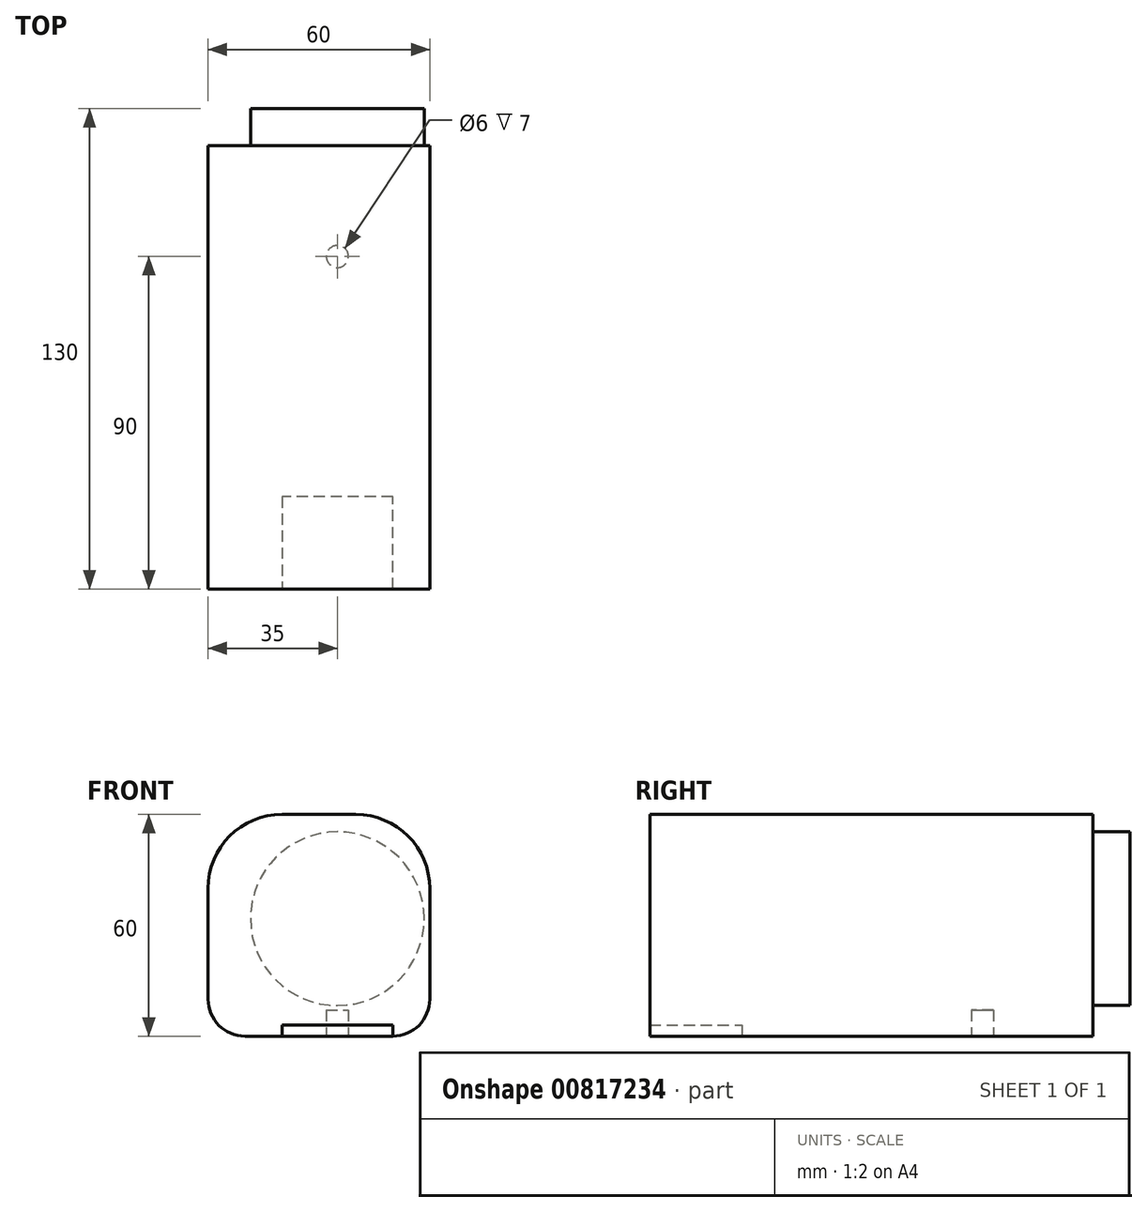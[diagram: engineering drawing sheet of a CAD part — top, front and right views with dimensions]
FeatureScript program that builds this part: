
annotation { "Feature Type Name" : "Feature", "Feature Type Description" : "" }
export const myFeature = defineFeature(function(context is Context, id is Id, definition is map)
    precondition{}
    {
        {
            var Q0;
            Q0=qCreatedBy(makeId("Top.planeOp"),FACE);
            var sketch = newSketch(context, id + "F0", { "sketchPlane" : qUnion([Q0])});
            skLineSegment(sketch, "E0.bottom", {"start": v(30, -60) * mm, "end": v(-30, -60) * mm});
            skLineSegment(sketch, "E0.top", {"start": v(30, 60) * mm, "end": v(-30, 60) * mm});
            skLineSegment(sketch, "E0.left", {"start": v(30, -60) * mm, "end": v(30, 60) * mm});
            skLineSegment(sketch, "E0.right", {"start": v(-30, -60) * mm, "end": v(-30, 60) * mm});
            skPoint(sketch, "E0.middle", {"position": v(0, 0) * mm});
            skSolve(sketch);
        }
        {
            var Q0;
            Q0=qSketchRegion(id+"F0",true);
            extrude(context, id + "F1", {"entities" : qUnion([Q0]), "depth" : 60 * mm, "offsetDistance" : 25 * mm});
        }
        {
            var Q0;
            Q0=makeQuery(id+"F1.opExtrude","CAP_FACE",FACE,{"disambiguationData":[OSD([sQuery(id+"F0.wireOp",EDGE,"E0.bottom"),sQuery(id+"F0.wireOp",EDGE,"E0.top"),sQuery(id+"F0.wireOp",EDGE,"E0.left"),sQuery(id+"F0.wireOp",EDGE,"E0.right")])],"isStart":true});
            var sketch = newSketch(context, id + "F2", { "sketchPlane" : qUnion([Q0])});
            skCircle(sketch, "E1", {"center": v(5, -30) * mm, "radius": 3 * mm});
            skSolve(sketch);
        }
        {
            var Q0;
            Q0=qSketchRegion(id+"F2",true);
            extrude(context, id + "F3", {"entities" : qUnion([Q0]), "operationType" : NewBodyOperationType.REMOVE, "oppositeDirection" : true, "depth" : 7 * mm, "offsetDistance" : 25 * mm});
        }
        {
            var Q0;
            Q0=makeQuery(id+"F1.opExtrude","CAP_EDGE",EDGE,{"disambiguationData":[OSD([sQuery(id+"F0.wireOp",EDGE,"E0.left")])],"isStart":false});
            var Q1;
            Q1=makeQuery(id+"F1.opExtrude","CAP_EDGE",EDGE,{"disambiguationData":[OSD([sQuery(id+"F0.wireOp",EDGE,"E0.right")])],"isStart":false});
            fillet(context, id + "F4", {"entities" : qUnion([Q0, Q1]), "radius" : 20 * mm, "tangentPropagation" : true, "allowEdgeOverflow" : false});
        }
        {
            var Q0;
            Q0=makeQuery(id+"F1.opExtrude","CAP_EDGE",EDGE,{"disambiguationData":[OSD([sQuery(id+"F0.wireOp",EDGE,"E0.left")])],"isStart":true});
            var Q1;
            Q1=makeQuery(id+"F1.opExtrude","CAP_EDGE",EDGE,{"disambiguationData":[OSD([sQuery(id+"F0.wireOp",EDGE,"E0.right")])],"isStart":true});
            fillet(context, id + "F5", {"entities" : qUnion([Q0, Q1]), "radius" : 10 * mm, "tangentPropagation" : true, "allowEdgeOverflow" : false});
        }
        {
            var Q0;
            Q0=makeQuery(id+"F1.opExtrude","SWEPT_FACE",FACE,{"disambiguationData":[OSD([sQuery(id+"F0.wireOp",EDGE,"E0.top")])]});
            var sketch = newSketch(context, id + "F6", { "sketchPlane" : qUnion([Q0])});
            skCircle(sketch, "E2", {"center": v(-5, 31.78) * mm, "radius": 23.5 * mm});
            skSolve(sketch);
        }
        {
            var Q0;
            Q0=qSketchRegion(id+"F6",true);
            extrude(context, id + "F7", {"entities" : qUnion([Q0]), "depth" : 10 * mm, "offsetDistance" : 25 * mm});
        }
        {
            var Q0;
            Q0=makeQuery(id+"F1.opExtrude","CAP_FACE",FACE,{"disambiguationData":[OSD([sQuery(id+"F0.wireOp",EDGE,"E0.bottom"),sQuery(id+"F0.wireOp",EDGE,"E0.top"),sQuery(id+"F0.wireOp",EDGE,"E0.left"),sQuery(id+"F0.wireOp",EDGE,"E0.right")])],"isStart":true});
            var sketch = newSketch(context, id + "F8", { "sketchPlane" : qUnion([Q0])});
            skLineSegment(sketch, "E3.bottom", {"start": v(20, 35) * mm, "end": v(-10, 35) * mm});
            skLineSegment(sketch, "E3.top", {"start": v(20, 60) * mm, "end": v(-10, 60) * mm});
            skLineSegment(sketch, "E3.left", {"start": v(20, 35) * mm, "end": v(20, 60) * mm});
            skLineSegment(sketch, "E3.right", {"start": v(-10, 35) * mm, "end": v(-10, 60) * mm});
            skSolve(sketch);
        }
        {
            var Q0;
            Q0=qSketchRegion(id+"F8",true);
            extrude(context, id + "F9", {"entities" : qUnion([Q0]), "operationType" : NewBodyOperationType.REMOVE, "oppositeDirection" : true, "depth" : 3 * mm, "offsetDistance" : 25 * mm});
        }
    });
